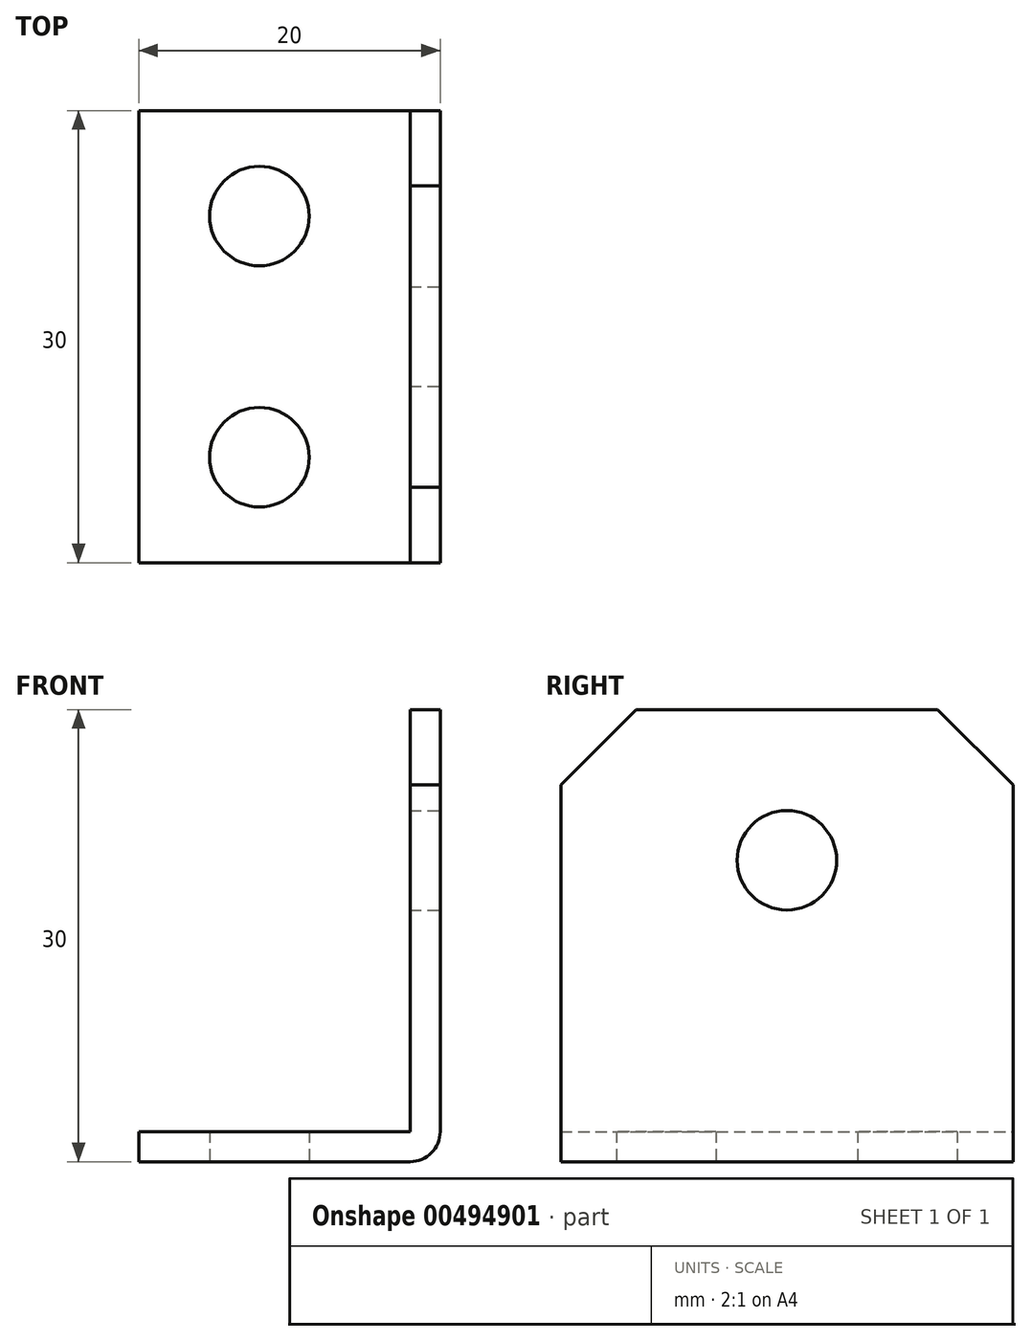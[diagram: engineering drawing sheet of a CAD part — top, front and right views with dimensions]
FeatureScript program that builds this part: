
annotation { "Feature Type Name" : "Feature", "Feature Type Description" : "" }
export const myFeature = defineFeature(function(context is Context, id is Id, definition is map)
    precondition{}
    {
        {
            var Q0;
            Q0=qCreatedBy(makeId("Front.planeOp"),FACE);
            var sketch = newSketch(context, id + "F0", { "sketchPlane" : qUnion([Q0])});
            skLineSegment(sketch, "E0", {"start": v(0, 0) * mm, "end": v(0, 30) * mm});
            skLineSegment(sketch, "E1", {"start": v(0, 30) * mm, "end": v(-2, 30) * mm});
            skLineSegment(sketch, "E2", {"start": v(-2, 2) * mm, "end": v(-20, 2) * mm});
            skLineSegment(sketch, "E3", {"start": v(0, 0) * mm, "end": v(-20, 0) * mm});
            skLineSegment(sketch, "E4", {"start": v(-20, 2) * mm, "end": v(-20, 0) * mm});
            skLineSegment(sketch, "E5", {"start": v(-2, 2) * mm, "end": v(-2, 30) * mm});
            skSolve(sketch);
        }
        {
            var Q0;
            Q0=qSketchRegion(id+"F0",true);
            extrude(context, id + "F1", {"entities" : qUnion([Q0]), "depth" : 30 * mm});
        }
        {
            var Q0;
            Q0=makeQuery(id+"F1.opExtrude","SWEPT_FACE",FACE,{"disambiguationData":[OSD([sQuery(id+"F0.wireOp",EDGE,"E3")])]});
            var sketch = newSketch(context, id + "F2", { "sketchPlane" : qUnion([Q0])});
            skPoint(sketch, "E6", {"position": v(-12, 23) * mm});
            skPoint(sketch, "E7", {"position": v(-12, 7) * mm});
            skSolve(sketch);
        }
        {
            var Q0;
            Q0=sQuery(id+"F2.wireOp",VERTEX,"E6");
            var Q1;
            Q1=sQuery(id+"F2.wireOp",VERTEX,"E7");
            var Q2;
            Q2=makeQuery(id+"F1.opExtrude","SWEPT_BODY",BODY,{"disambiguationData":[OSD([sQuery(id+"F0.wireOp",EDGE,"E0"),sQuery(id+"F0.wireOp",EDGE,"E1"),sQuery(id+"F0.wireOp",EDGE,"E2"),sQuery(id+"F0.wireOp",EDGE,"E3"),sQuery(id+"F0.wireOp",EDGE,"E4"),sQuery(id+"F0.wireOp",EDGE,"E5")])]});
            hole(context, id + "F3", {"style" : HoleStyle.SIMPLE, "endStyle" : HoleEndStyle.THROUGH, "standardTappedOrClearance" : lookupTablePath({ "standard" : "ISO", "size" : "6.6", "type" : "Drilled" }), "standardBlindInLast" : lookupTablePath({ "standard" : "ISO", "size" : "6.6", "type" : "Drilled" }), "holeDiameter" : 6.6 * mm, "isTappedThrough" : true, "tappedDepth" : 10 * mm, "tapClearance" : 3, "locations" : qUnion([Q0, Q1]), "scope" : qUnion([Q2])});
        }
        {
            var Q0;
            Q0=makeQuery(id+"F1.opExtrude","SWEPT_FACE",FACE,{"disambiguationData":[OSD([sQuery(id+"F0.wireOp",EDGE,"E0")])]});
            var sketch = newSketch(context, id + "F4", { "sketchPlane" : qUnion([Q0])});
            skPoint(sketch, "E8", {"position": v(-15, 20) * mm});
            skSolve(sketch);
        }
        {
            var Q0;
            Q0=sQuery(id+"F4.wireOp",VERTEX,"E8");
            var Q1;
            Q1=makeQuery(id+"F1.opExtrude","SWEPT_BODY",BODY,{"disambiguationData":[OSD([sQuery(id+"F0.wireOp",EDGE,"E0"),sQuery(id+"F0.wireOp",EDGE,"E1"),sQuery(id+"F0.wireOp",EDGE,"E2"),sQuery(id+"F0.wireOp",EDGE,"E3"),sQuery(id+"F0.wireOp",EDGE,"E4"),sQuery(id+"F0.wireOp",EDGE,"E5")])]});
            hole(context, id + "F5", {"style" : HoleStyle.SIMPLE, "endStyle" : HoleEndStyle.THROUGH, "standardTappedOrClearance" : lookupTablePath({ "standard" : "ISO", "size" : "6.6", "type" : "Drilled" }), "standardBlindInLast" : lookupTablePath({ "standard" : "ISO", "size" : "6.6", "type" : "Drilled" }), "holeDiameter" : 6.6 * mm, "isTappedThrough" : true, "tappedDepth" : 10 * mm, "tapClearance" : 3, "locations" : qUnion([Q0]), "scope" : qUnion([Q1])});
        }
        {
            var Q0;
            Q0=makeQuery(id+"F1.opExtrude","SWEPT_EDGE",EDGE,{"disambiguationData":[OSD([sQuery(id+"F0.wireOp",EDGE,"E0"),sQuery(id+"F0.wireOp",EDGE,"E3")])]});
            fillet(context, id + "F6", {"entities" : qUnion([Q0]), "radius" : 2 * mm, "tangentPropagation" : true, "allowEdgeOverflow" : false});
        }
        {
            var Q0;
            Q0=makeQuery(id+"F1.opExtrude","CAP_EDGE",EDGE,{"disambiguationData":[OSD([sQuery(id+"F0.wireOp",EDGE,"E1")])],"isStart":false});
            var Q1;
            Q1=makeQuery(id+"F1.opExtrude","CAP_EDGE",EDGE,{"disambiguationData":[OSD([sQuery(id+"F0.wireOp",EDGE,"E1")])],"isStart":true});
            chamfer(context, id + "F7", {"entities" : qUnion([Q0, Q1]), "width" : 5 * mm, "tangentPropagation" : true});
        }
    });
